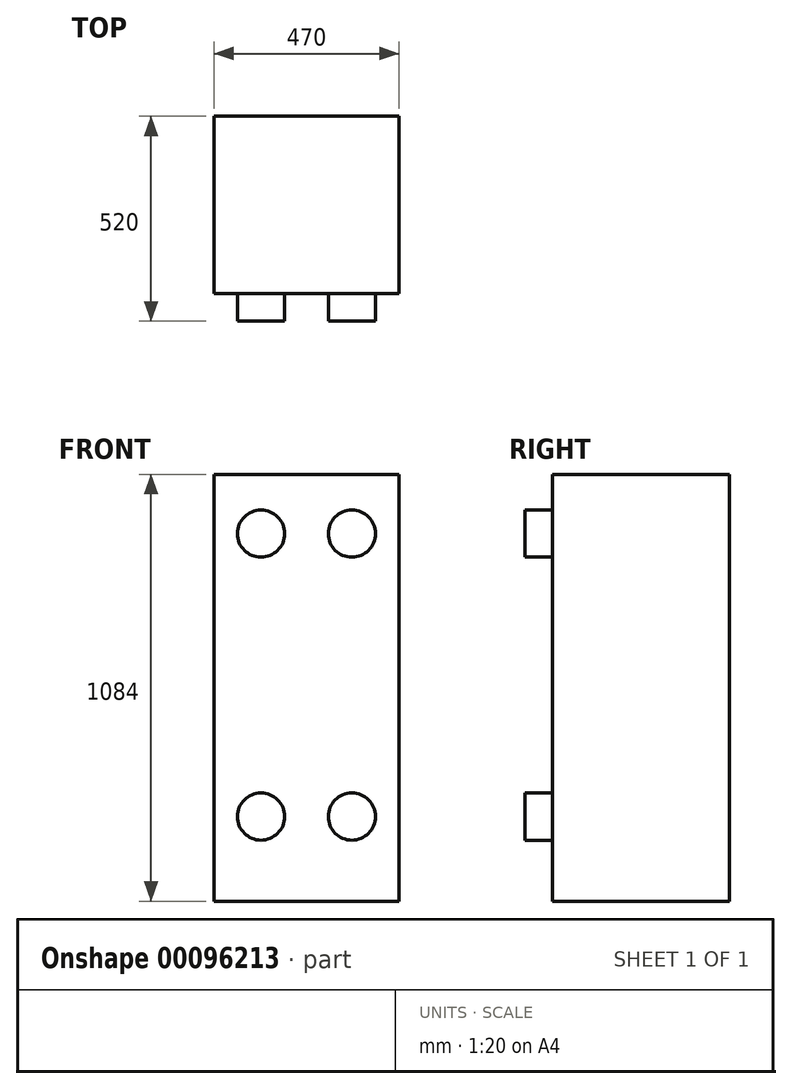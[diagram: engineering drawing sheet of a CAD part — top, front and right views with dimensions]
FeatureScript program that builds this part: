
annotation { "Feature Type Name" : "Feature", "Feature Type Description" : "" }
export const myFeature = defineFeature(function(context is Context, id is Id, definition is map)
    precondition{}
    {
        {
            var Q0;
            Q0=qCreatedBy(makeId("Front.planeOp"),FACE);
            var sketch = newSketch(context, id + "F0", { "sketchPlane" : qUnion([Q0])});
            skLineSegment(sketch, "E0.bottom", {"start": v(235, 542) * mm, "end": v(-235, 542) * mm});
            skLineSegment(sketch, "E0.top", {"start": v(235, -542) * mm, "end": v(-235, -542) * mm});
            skLineSegment(sketch, "E0.left", {"start": v(235, 542) * mm, "end": v(235, -542) * mm});
            skLineSegment(sketch, "E0.right", {"start": v(-235, 542) * mm, "end": v(-235, -542) * mm});
            skPoint(sketch, "E0.middle", {"position": v(0, 0) * mm});
            skSolve(sketch);
        }
        {
            var Q0;
            Q0 = qSketchRegion(id + "F0", true);
            extrude(context, id + "F1", {"entities" : qUnion([Q0]), "endBound" : BoundingType.SYMMETRIC, "depth" : 450 * mm});
        }
        {
            var Q0;
            Q0=makeQuery(id+"F1.opExtrude","CAP_FACE",FACE,{"disambiguationData":[OSD([sQuery(id+"F0.wireOp",EDGE,"E0.bottom"),sQuery(id+"F0.wireOp",EDGE,"E0.top"),sQuery(id+"F0.wireOp",EDGE,"E0.left"),sQuery(id+"F0.wireOp",EDGE,"E0.right")])],"isStart":false});
            var sketch = newSketch(context, id + "F2", { "sketchPlane" : qUnion([Q0])});
            skCircle(sketch, "E1", {"center": v(-115.5, 392) * mm, "radius": 60 * mm});
            skCircle(sketch, "E2.0.1.0", {"center": v(-115.5, -327) * mm, "radius": 60 * mm});
            skCircle(sketch, "E2.1.0.0", {"center": v(115.5, 392) * mm, "radius": 60 * mm});
            skCircle(sketch, "E2.1.1.0", {"center": v(115.5, -327) * mm, "radius": 60 * mm});
            skLineSegment(sketch, "E2.direction1", {"start": v(-115.5, 392) * mm, "end": v(115.5, 392) * mm, "construction": true});
            skLineSegment(sketch, "E2.direction2", {"start": v(-115.5, 392) * mm, "end": v(-115.5, -327) * mm, "construction": true});
            skSolve(sketch);
        }
        {
            var Q0;
            Q0 = qSketchRegion(id + "F2", true);
            extrude(context, id + "F3", {"entities" : qUnion([Q0]), "operationType" : NewBodyOperationType.ADD, "depth" : 70 * mm});
        }
    });
